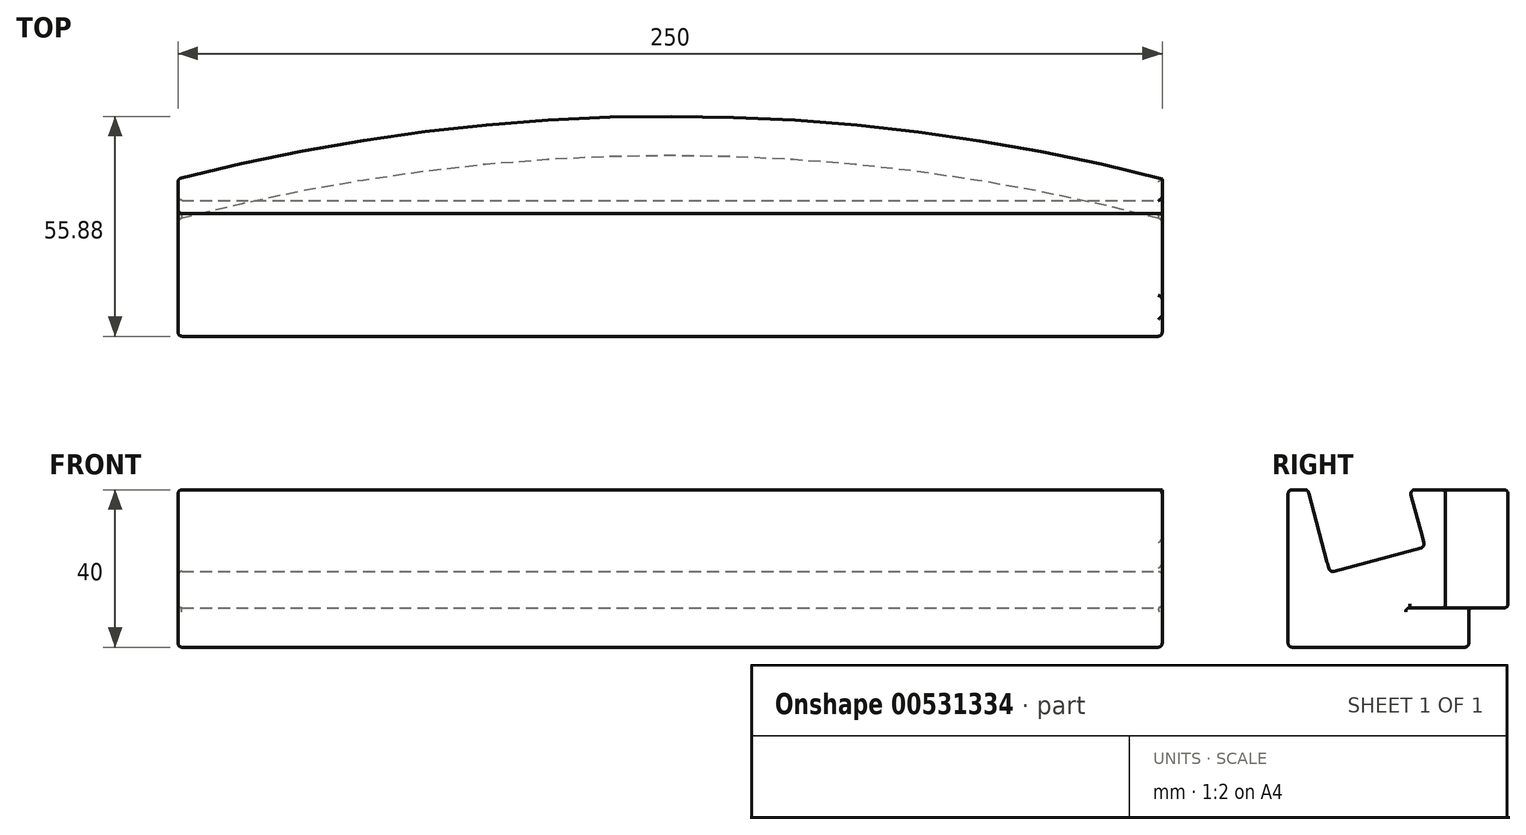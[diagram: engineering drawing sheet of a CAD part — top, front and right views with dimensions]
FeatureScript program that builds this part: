
annotation { "Feature Type Name" : "Feature", "Feature Type Description" : "" }
export const myFeature = defineFeature(function(context is Context, id is Id, definition is map)
    precondition{}
    {
        {
            var Q0;
            Q0=qCreatedBy(makeId("Top.planeOp"),FACE);
            var sketch = newSketch(context, id + "F0", { "sketchPlane" : qUnion([Q0])});
            skLineSegment(sketch, "E0.bottom", {"start": v(-125, 40) * mm, "end": v(125, 40) * mm, "construction": true});
            skLineSegment(sketch, "E0.top", {"start": v(-125, 0) * mm, "end": v(125, 0) * mm});
            skLineSegment(sketch, "E0.left", {"start": v(-125, 40) * mm, "end": v(-125, 0) * mm});
            skLineSegment(sketch, "E0.right", {"start": v(125, 40) * mm, "end": v(125, 0) * mm});
            skLineSegment(sketch, "E1", {"start": v(0, 0) * mm, "end": v(0, 55.88) * mm, "construction": true});
            skArc(sketch, "E2", {"start": v(125, 40) * mm, "mid": v(0, 55.88) * mm, "end": v(-125, 40) * mm});
            skSolve(sketch);
        }
        {
            var Q0;
            Q0 = qSketchRegion(id + "F0", true);
            extrude(context, id + "F1", {"entities" : qUnion([Q0]), "depth" : 40 * mm, "offsetDistance" : 25 * mm});
        }
        {
            var Q0;
            Q0=makeQuery(id+"F1.opExtrude","SWEPT_FACE",FACE,{"disambiguationData":[OSD([sQuery(id+"F0.wireOp",EDGE,"E0.right")])]});
            var sketch = newSketch(context, id + "F2", { "sketchPlane" : qUnion([Q0])});
            skLineSegment(sketch, "E3.top", {"start": v(10.62, 19.04) * mm, "end": v(34.76, 25.51) * mm});
            skLineSegment(sketch, "E3.right", {"start": v(30.88, 40) * mm, "end": v(34.76, 25.51) * mm});
            skLineSegment(sketch, "E4", {"start": v(10.62, 19.04) * mm, "end": v(5, 40) * mm});
            skLineSegment(sketch, "E5", {"start": v(5, 40) * mm, "end": v(30.88, 40) * mm});
            skSolve(sketch);
        }
        {
            var Q0;
            Q0=makeQuery(id+"F2.imprint","IMPRINT",FACE,{"disambiguationData":[TD([[makeQuery(id+"F2.imprint","IMPRINT",EDGE,{"derivedFrom":sQuery(id+"F2.wireOp",EDGE,"E3.top")}),1.0]])]});
            extrude(context, id + "F3", {"entities" : qUnion([Q0]), "operationType" : NewBodyOperationType.REMOVE, "endBound" : BoundingType.THROUGH_ALL, "oppositeDirection" : true, "depth" : 25 * mm, "offsetDistance" : 25 * mm});
        }
        {
            var Q0;
            Q0=makeQuery(id+"F1.opExtrude","CAP_FACE",FACE,{"disambiguationData":[OSD([sQuery(id+"F0.wireOp",EDGE,"E0.top"),sQuery(id+"F0.wireOp",EDGE,"E0.left"),sQuery(id+"F0.wireOp",EDGE,"E0.right"),sQuery(id+"F0.wireOp",EDGE,"E2")])],"isStart":true});
            var sketch = newSketch(context, id + "F4", { "sketchPlane" : qUnion([Q0])});
            skArc(sketch, "E6.0", {"start": v(125, -29.67) * mm, "mid": v(0, -45.88) * mm, "end": v(-125, -29.67) * mm});
            skLineSegment(sketch, "E7.0", {"start": v(-125, -10) * mm, "end": v(125, -10) * mm});
            skSolve(sketch);
        }
        {
            var Q0;
            {var subQ0=sQuery(id+"F4.wireOp",EDGE,"E6.0");Q0=makeQuery(id+"F4.imprint","IMPRINT",FACE,{"disambiguationData":[TD([[makeQuery(id+"F4.imprint","IMPRINT",EDGE,{"derivedFrom":subQ0}),-1.0]])]});}
            extrude(context, id + "F5", {"entities" : qUnion([Q0]), "operationType" : NewBodyOperationType.REMOVE, "oppositeDirection" : true, "depth" : 10 * mm, "offsetDistance" : 25 * mm});
        }
        {
            var Q0;
            Q0=makeQuery(id+"F1.opExtrude","CAP_EDGE",EDGE,{"disambiguationData":[OSD([sQuery(id+"F0.wireOp",EDGE,"E2")])],"isStart":false});
            var Q1;
            Q1=makeQuery(id+"F3.boolean.opBoolean","COPY",EDGE,{"derivedFrom":makeQuery(id+"F3.opExtrude","SWEPT_EDGE",EDGE,{"disambiguationData":[OSD([sQuery(id+"F0.wireOp",EDGE,"E0.right"),sQuery(id+"F2.wireOp",EDGE,"E3.right"),sQuery(id+"F2.wireOp",EDGE,"E5")])]})});
            var Q2;
            {var subQ0=sQuery(id+"F0.wireOp",EDGE,"E2");var subQ1=sQuery(id+"F0.wireOp",EDGE,"E0.left");Q2=makeQuery(id+"F3.boolean.opBoolean","SPLIT",EDGE,{"disambiguationData":[TD([makeQuery(id+"F1.opExtrude","SWEPT_FACE",FACE,{"disambiguationData":[OSD([subQ0])]})])],"derivedFrom":makeQuery(id+"F1.opExtrude","CAP_EDGE",EDGE,{"disambiguationData":[OSD([subQ1])],"isStart":false})});}
            var Q3;
            Q3=makeQuery(id+"F1.opExtrude","SWEPT_FACE",FACE,{"disambiguationData":[OSD([sQuery(id+"F0.wireOp",EDGE,"E0.left")])]});
            var Q4;
            Q4=makeQuery(id+"F3.boolean.opBoolean","COPY",FACE,{"derivedFrom":makeQuery(id+"F3.opExtrude","SWEPT_FACE",FACE,{"disambiguationData":[OSD([sQuery(id+"F2.wireOp",EDGE,"E3.top")])]})});
            var Q5;
            {var subQ0=sQuery(id+"F0.wireOp",EDGE,"E0.top");var subQ1=sQuery(id+"F0.wireOp",EDGE,"E0.left");var subQ2=sQuery(id+"F0.wireOp",EDGE,"E0.right");Q5=makeQuery(id+"F3.boolean.opBoolean","SPLIT",FACE,{"disambiguationData":[TD([makeQuery(id+"F1.opExtrude","SWEPT_FACE",FACE,{"disambiguationData":[OSD([subQ0])]})])],"derivedFrom":makeQuery(id+"F1.opExtrude","CAP_FACE",FACE,{"disambiguationData":[OSD([subQ0,subQ1,subQ2,sQuery(id+"F0.wireOp",EDGE,"E2")])],"isStart":false})});}
            var Q6;
            Q6=makeQuery(id+"F5.boolean.opBoolean","COPY",FACE,{"derivedFrom":makeQuery(id+"F5.opExtrude","CAP_FACE",FACE,{"disambiguationData":[OSD([sQuery(id+"F0.wireOp",EDGE,"E0.left"),sQuery(id+"F0.wireOp",EDGE,"E0.right"),sQuery(id+"F4.wireOp",EDGE,"E6.0"),sQuery(id+"F4.wireOp",EDGE,"E7.0")])],"isStart":false})});
            var Q7;
            Q7=makeQuery(id+"F5.boolean.opBoolean","COPY",FACE,{"derivedFrom":makeQuery(id+"F5.opExtrude","SWEPT_FACE",FACE,{"disambiguationData":[OSD([sQuery(id+"F4.wireOp",EDGE,"E6.0")])]})});
            var Q8;
            {var subQ0=sQuery(id+"F0.wireOp",EDGE,"E0.left");var subQ1=sQuery(id+"F0.wireOp",EDGE,"E0.right");var subQ2=sQuery(id+"F0.wireOp",EDGE,"E2");Q8=makeQuery(id+"F5.boolean.opBoolean","SPLIT",FACE,{"disambiguationData":[TD([makeQuery(id+"F1.opExtrude","SWEPT_FACE",FACE,{"disambiguationData":[OSD([subQ2])]})])],"derivedFrom":makeQuery(id+"F1.opExtrude","CAP_FACE",FACE,{"disambiguationData":[OSD([sQuery(id+"F0.wireOp",EDGE,"E0.top"),subQ0,subQ1,subQ2])],"isStart":true})});}
            var Q9;
            {var subQ0=sQuery(id+"F0.wireOp",EDGE,"E0.top");var subQ1=sQuery(id+"F0.wireOp",EDGE,"E0.left");var subQ2=sQuery(id+"F0.wireOp",EDGE,"E0.right");Q9=makeQuery(id+"F5.boolean.opBoolean","SPLIT",FACE,{"disambiguationData":[TD([makeQuery(id+"F1.opExtrude","SWEPT_FACE",FACE,{"disambiguationData":[OSD([subQ0])]})])],"derivedFrom":makeQuery(id+"F1.opExtrude","CAP_FACE",FACE,{"disambiguationData":[OSD([subQ0,subQ1,subQ2,sQuery(id+"F0.wireOp",EDGE,"E2")])],"isStart":true})});}
            var Q10;
            Q10=makeQuery(id+"F1.opExtrude","SWEPT_FACE",FACE,{"disambiguationData":[OSD([sQuery(id+"F0.wireOp",EDGE,"E0.top")])]});
            fillet(context, id + "F6", {"entities" : qUnion([Q0, Q1, Q2, Q3, Q4, Q5, Q6, Q7, Q8, Q9, Q10]), "radius" : 1 * mm, "tangentPropagation" : true, "allowEdgeOverflow" : false});
        }
    });
